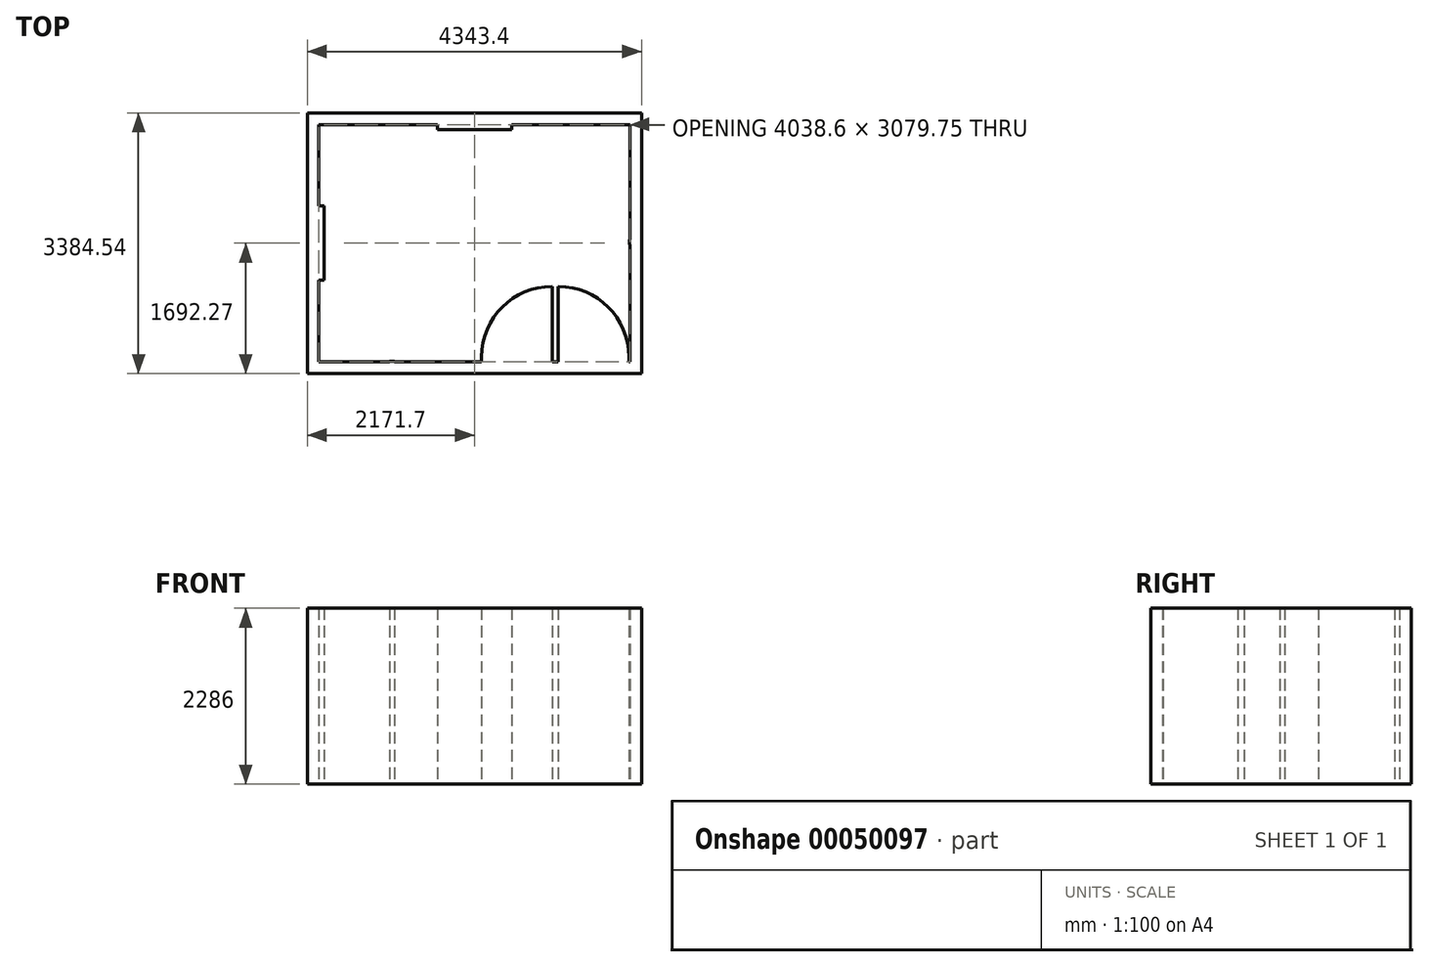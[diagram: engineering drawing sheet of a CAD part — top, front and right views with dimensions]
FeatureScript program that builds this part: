
annotation { "Feature Type Name" : "Feature", "Feature Type Description" : "" }
export const myFeature = defineFeature(function(context is Context, id is Id, definition is map)
    precondition{}
    {
        {
            var Q0;
            Q0=qCreatedBy(makeId("Top.planeOp"), FACE);
            var sketch = newSketch(context, id + "F0", { "sketchPlane" : qUnion([Q0])});
            skLineSegment(sketch, "E0.bottom", {"start": v(-2019.3, 1539.87) * mm, "end": v(-482.6, 1539.87) * mm});
            skLineSegment(sketch, "E0.top", {"start": v(-2019.3, -1539.88) * mm, "end": v(-1104.9, -1539.88) * mm});
            skLineSegment(sketch, "E0.left", {"start": v(-2019.3, 1539.87) * mm, "end": v(-2019.3, 485.77) * mm});
            skLineSegment(sketch, "E0.right", {"start": v(2019.3, 1539.87) * mm, "end": v(2019.3, 47.63) * mm});
            skLineSegment(sketch, "E1.bottom", {"start": v(-2171.7, 1692.27) * mm, "end": v(2171.7, 1692.27) * mm});
            skLineSegment(sketch, "E1.top", {"start": v(-2171.7, -1692.28) * mm, "end": v(2171.7, -1692.28) * mm});
            skLineSegment(sketch, "E1.left", {"start": v(-2171.7, 1692.27) * mm, "end": v(-2171.7, -1692.28) * mm});
            skLineSegment(sketch, "E1.right", {"start": v(2171.7, 1692.27) * mm, "end": v(2171.7, -1692.28) * mm});
            skLineSegment(sketch, "E2", {"start": v(-2019.3, 485.77) * mm, "end": v(-1955.8, 485.77) * mm});
            skLineSegment(sketch, "E3", {"start": v(-1955.8, 485.77) * mm, "end": v(-1955.8, -479.43) * mm});
            skLineSegment(sketch, "E4", {"start": v(-1955.8, -479.43) * mm, "end": v(-2019.3, -479.43) * mm});
            skLineSegment(sketch, "E5", {"start": v(95.25, -1539.88) * mm, "end": v(95.25, -1476.38) * mm});
            skLineSegment(sketch, "E6", {"start": v(1009.65, -1476.38) * mm, "end": v(1009.65, -1539.88) * mm});
            skLineSegment(sketch, "E7", {"start": v(1092.2, -1539.88) * mm, "end": v(1092.2, -1476.38) * mm});
            skLineSegment(sketch, "E8", {"start": v(2006.6, -1476.38) * mm, "end": v(2006.6, -1539.88) * mm});
            skLineSegment(sketch, "E9", {"start": v(-482.6, 1539.88) * mm, "end": v(-482.6, 1476.38) * mm});
            skLineSegment(sketch, "E10", {"start": v(-482.6, 1476.37) * mm, "end": v(482.6, 1476.37) * mm});
            skLineSegment(sketch, "E11", {"start": v(482.6, 1476.38) * mm, "end": v(482.6, 1539.88) * mm});
            skLineSegment(sketch, "E12", {"start": v(2019.3, 47.63) * mm, "end": v(2012.95, 47.63) * mm});
            skLineSegment(sketch, "E13", {"start": v(2012.95, 47.63) * mm, "end": v(2012.95, -15.87) * mm});
            skLineSegment(sketch, "E14", {"start": v(2012.95, -15.87) * mm, "end": v(2019.3, -15.87) * mm});
            skLineSegment(sketch, "E15", {"start": v(-1104.9, -1539.88) * mm, "end": v(-1104.9, -1533.53) * mm});
            skLineSegment(sketch, "E16", {"start": v(-1104.9, -1533.53) * mm, "end": v(-1041.4, -1533.53) * mm});
            skLineSegment(sketch, "E17", {"start": v(-1041.4, -1533.53) * mm, "end": v(-1041.4, -1539.88) * mm});
            skLineSegment(sketch, "E18.trimOffspring", {"start": v(-2019.3, -479.43) * mm, "end": v(-2019.3, -1539.88) * mm});
            skLineSegment(sketch, "E19.trimOffspring", {"start": v(482.6, 1539.87) * mm, "end": v(2019.3, 1539.87) * mm});
            skLineSegment(sketch, "E20.trimOffspring", {"start": v(2019.3, -15.87) * mm, "end": v(2019.3, -1539.88) * mm});
            skLineSegment(sketch, "E21.trimOffspring", {"start": v(2006.6, -1539.88) * mm, "end": v(2019.3, -1539.88) * mm});
            skLineSegment(sketch, "E22.trimOffspring", {"start": v(1009.65, -1539.88) * mm, "end": v(1092.2, -1539.88) * mm});
            skLineSegment(sketch, "E23.trimOffspring", {"start": v(-1041.4, -1539.88) * mm, "end": v(95.25, -1539.88) * mm});
            skLineSegment(sketch, "E24", {"start": v(1009.65, -1476.38) * mm, "end": v(1009.65, -561.97) * mm});
            skLineSegment(sketch, "E25", {"start": v(1092.2, -1476.38) * mm, "end": v(1092.2, -561.97) * mm});
            skArc(sketch, "E26", {"start": v(1009.65, -561.97) * mm, "mid": v(363.07, -829.8) * mm, "end": v(95.25, -1476.38) * mm});
            skArc(sketch, "E27", {"start": v(2006.6, -1476.38) * mm, "mid": v(1738.78, -829.8) * mm, "end": v(1092.2, -561.97) * mm});
            skSolve(sketch);
        }
        {
            var Q0;
            Q0 = qSketchRegion(id + "F0", true);
            extrude(context, id + "F1", {"entities" : qUnion([Q0]), "depth" : 2286 * mm, "offsetDistance" : 25.4 * mm});
        }
    });
